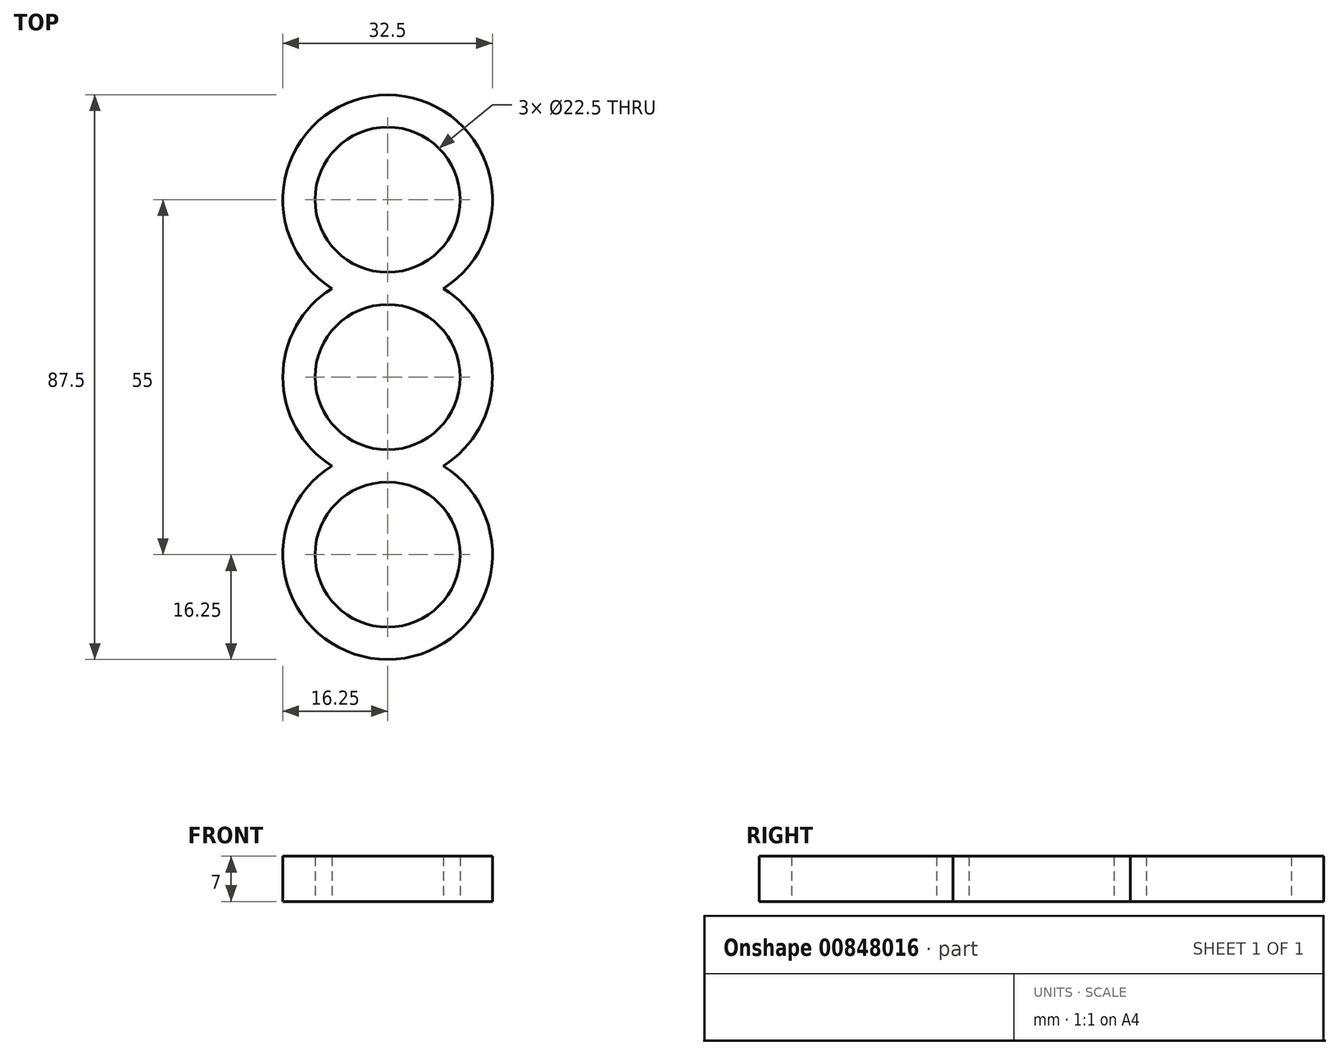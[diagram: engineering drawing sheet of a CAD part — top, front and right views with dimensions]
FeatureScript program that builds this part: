
annotation { "Feature Type Name" : "Feature", "Feature Type Description" : "" }
export const myFeature = defineFeature(function(context is Context, id is Id, definition is map)
    precondition{}
    {
        {
            var Q0;
            Q0=qCreatedBy(makeId("Top.planeOp"),FACE);
            var sketch = newSketch(context, id + "F0", { "sketchPlane" : qUnion([Q0])});
            skCircle(sketch, "E0", {"center": v(0, 0) * mm, "radius": 11.25 * mm});
            skCircle(sketch, "E1", {"center": v(0, 27.5) * mm, "radius": 11.25 * mm});
            skCircle(sketch, "E2", {"center": v(0, -27.5) * mm, "radius": 11.25 * mm});
            skArc(sketch, "E3", {"start": v(8.66, 13.75) * mm, "mid": v(0, 43.75) * mm, "end": v(-8.66, 13.75) * mm});
            skArc(sketch, "E4", {"start": v(-8.66, 13.75) * mm, "mid": v(-16.25, 0) * mm, "end": v(-8.66, -13.75) * mm});
            skArc(sketch, "E5", {"start": v(-8.66, -13.75) * mm, "mid": v(0, -43.75) * mm, "end": v(8.66, -13.75) * mm});
            skArc(sketch, "E6.trimOffspring", {"start": v(8.66, -13.75) * mm, "mid": v(16.25, 0) * mm, "end": v(8.66, 13.75) * mm});
            skSolve(sketch);
        }
        {
            var Q0;
            Q0 = qSketchRegion(id + "F0", true);
            extrude(context, id + "F1", {"entities" : qUnion([Q0]), "depth" : 7 * mm, "offsetDistance" : 25 * mm});
        }
    });
